# Revit family: Boiler-WeilMcLain-Aquabalance
name_source: partatom
category: Mechanical Equipment
revit_build: Autodesk Revit 2015 (Build: 20140606_1530(x64)
units: mm (PartAtom-declared; Revit-internal decimal feet)

## types (3) — shared parameters
Cold Water Supply = 1"
Combustion Air = 3"
Default Elevation = 4' - 0"
Depth = 1' - 0 19/32"
Description = Gas Boiler
Flue Outlet = 3"
Frequency = 60 Hz
Gas Connection = 1"
Heating System Return = 1"
Heating System Supply = 1"
Heating System Tapping = 0' - 0 3/8"
Height = 2' - 3 9/16"
Hot Water Outlet = 1"
Manufacturer = Weil-McLain
Number of Poles = 1
Phase = 1
Power Factor = 1
Product Documentation Link = http://aquabalanceboiler.com
Product Name = Aquabalance
Product Page URL = http://aquabalanceboiler.com
URL = https://www.weil-mclain.com
Voltage = 120 V
Width = 1' - 4 17/32"

## per-type parameters (varying)
| type | 2 | 3 | Actual Heating Water Flow |
| WMB-80 | 0' - 4 13/32" | 0' - 5 27/32" | 2 GPM |
| WMB-120 | 0' - 4 13/32" | 0' - 5 27/32" | 3 GPM |
| WMB-155 | 0' - 5 27/32" | 0' - 4 15/32" | 4 GPM |

note: column(s) folded — value = type name in every type: Model

## geometry (parser evidence)
native form markers: Blend x12, Sweep x2
no freeform markers — native parametric forms only
